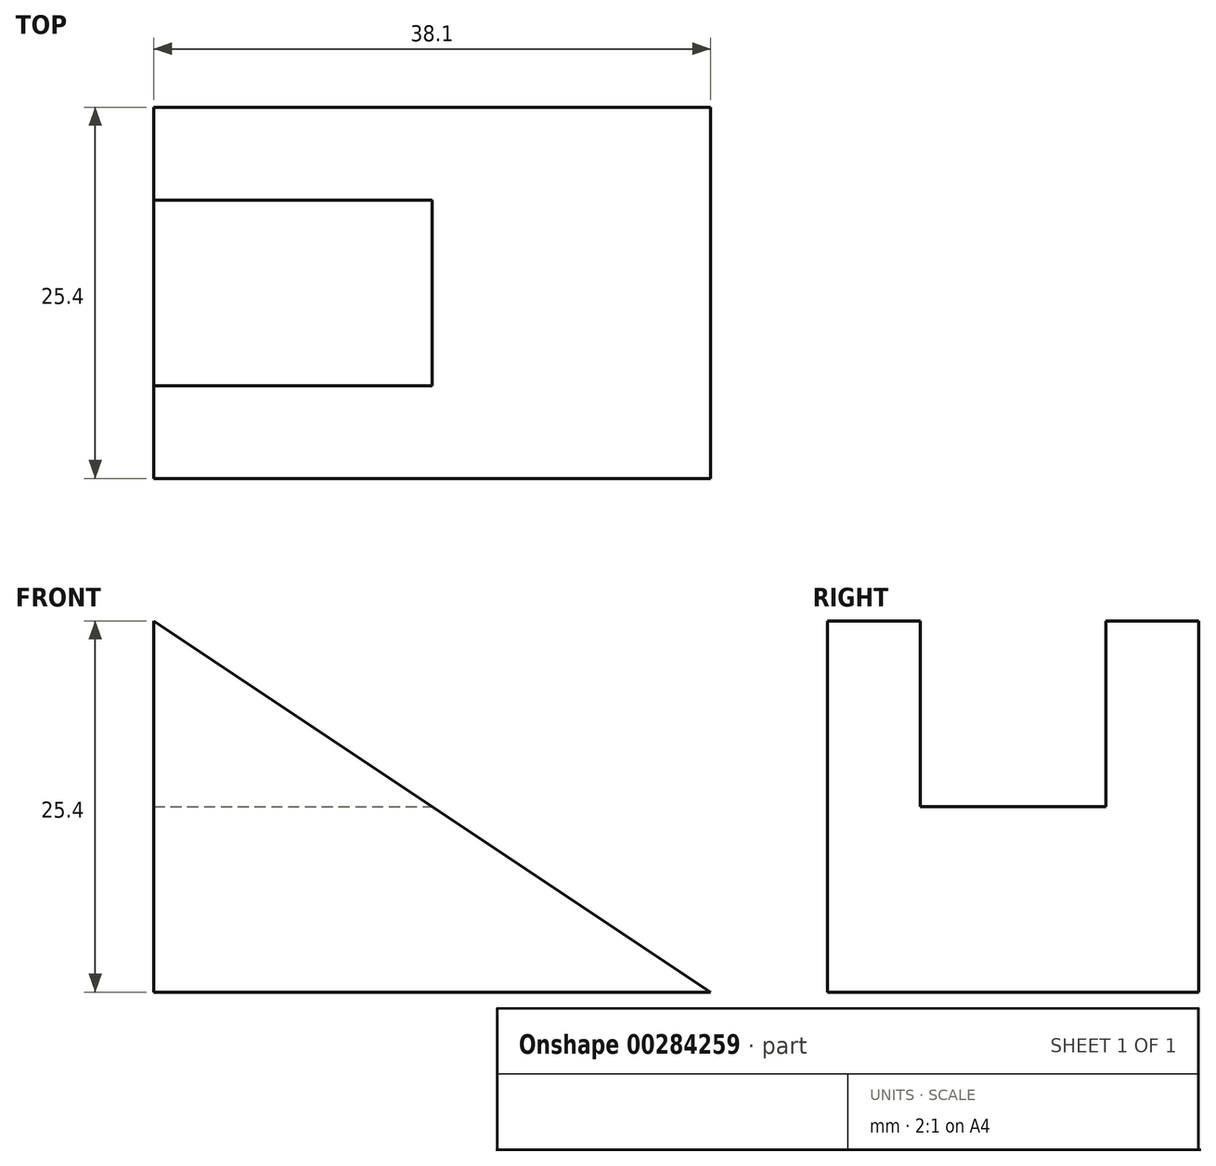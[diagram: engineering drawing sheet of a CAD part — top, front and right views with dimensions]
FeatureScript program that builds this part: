
annotation { "Feature Type Name" : "Feature", "Feature Type Description" : "" }
export const myFeature = defineFeature(function(context is Context, id is Id, definition is map)
    precondition{}
    {
        {
            var Q0;
            Q0=qCreatedBy(makeId("Front.planeOp"),FACE);
            var sketch = newSketch(context, id + "F0", { "sketchPlane" : qUnion([Q0])});
            skLineSegment(sketch, "E0", {"start": v(0, 0) * mm, "end": v(38.1, 0) * mm});
            skLineSegment(sketch, "E1", {"start": v(0, 0) * mm, "end": v(0, 25.4) * mm});
            skLineSegment(sketch, "E2", {"start": v(0, 25.4) * mm, "end": v(38.1, 0) * mm});
            skSolve(sketch);
        }
        {
            var Q0;
            Q0=makeQuery(id+"F0.imprint","IMPRINT",FACE,{"disambiguationData":[TD([[makeQuery(id+"F0.imprint","IMPRINT",EDGE,{"derivedFrom":sQuery(id+"F0.wireOp",EDGE,"E0")}),1.0]])]});
            extrude(context, id + "F1", {"entities" : qUnion([Q0]), "depth" : 25.4 * mm});
        }
        {
            var Q0;
            Q0=qCreatedBy(makeId("Front.planeOp"),FACE);
            var sketch = newSketch(context, id + "F2", { "sketchPlane" : qUnion([Q0])});
            skLineSegment(sketch, "E3", {"start": v(0, 25.4) * mm, "end": v(0, 12.7) * mm});
            skLineSegment(sketch, "E4", {"start": v(0, 12.7) * mm, "end": v(19.05, 12.7) * mm});
            skLineSegment(sketch, "E5", {"start": v(0, 25.4) * mm, "end": v(19.05, 12.7) * mm});
            skSolve(sketch);
        }
        {
            var Q0;
            Q0 = qSketchRegion(id + "F2", true);
            extrude(context, id + "F3", {"entities" : qUnion([Q0]), "operationType" : NewBodyOperationType.REMOVE, "depth" : 19.05 * mm, "hasSecondDirection" : true, "secondDirectionOppositeDirection" : false, "secondDirectionDepth" : 6.35 * mm});
        }
    });
